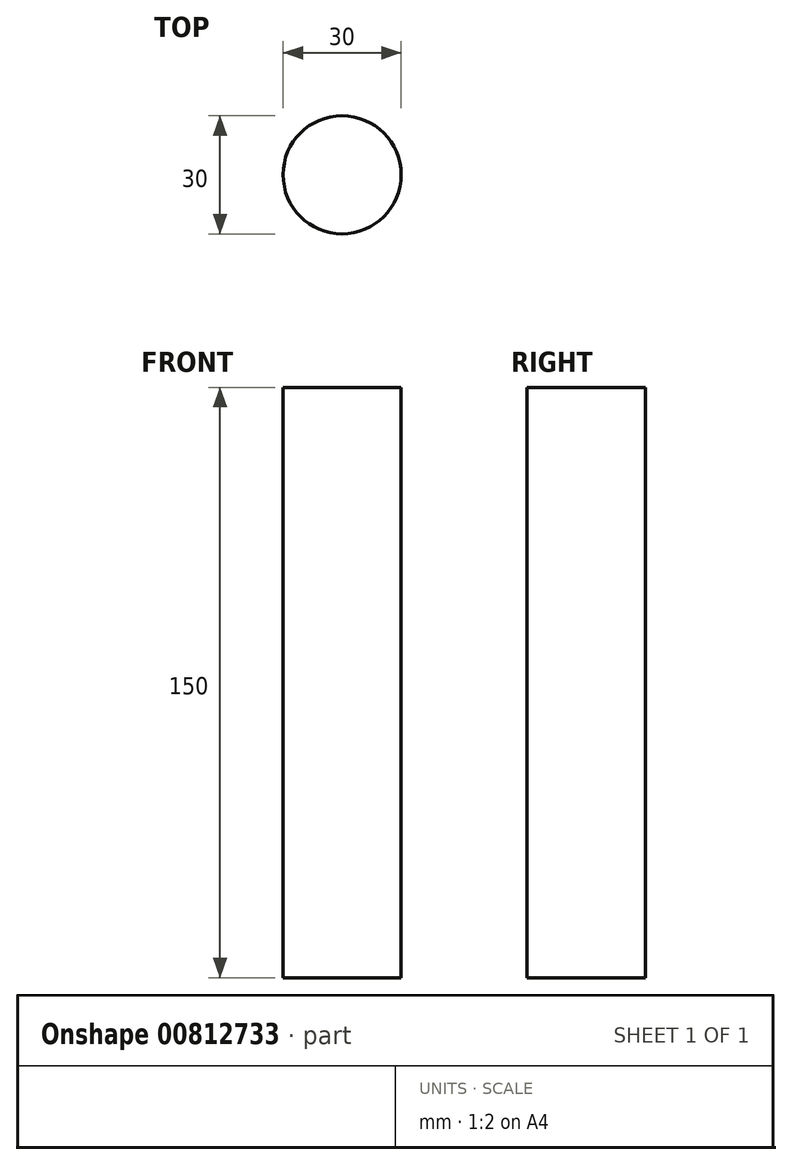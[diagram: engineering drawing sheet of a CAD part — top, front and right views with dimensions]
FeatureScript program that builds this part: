
annotation { "Feature Type Name" : "Feature", "Feature Type Description" : "" }
export const myFeature = defineFeature(function(context is Context, id is Id, definition is map)
    precondition{}
    {
        {
            var Q0;
            Q0=qCreatedBy(makeId("Top.planeOp"),FACE);
            var sketch = newSketch(context, id + "F0", { "sketchPlane" : qUnion([Q0])});
            skCircle(sketch, "E0", {"center": v(0, 0) * mm, "radius": 15 * mm});
            skSolve(sketch);
        }
        {
            var Q0;
            Q0=makeQuery(id+"F0.imprint","IMPRINT",FACE,{"disambiguationData":[TD([[makeQuery(id+"F0.imprint","IMPRINT",EDGE,{"derivedFrom":sQuery(id+"F0.wireOp",EDGE,"E0")}),1.0]])]});
            extrude(context, id + "F1", {"entities" : qUnion([Q0]), "depth" : 150 * mm, "offsetDistance" : 25 * mm});
        }
    });
